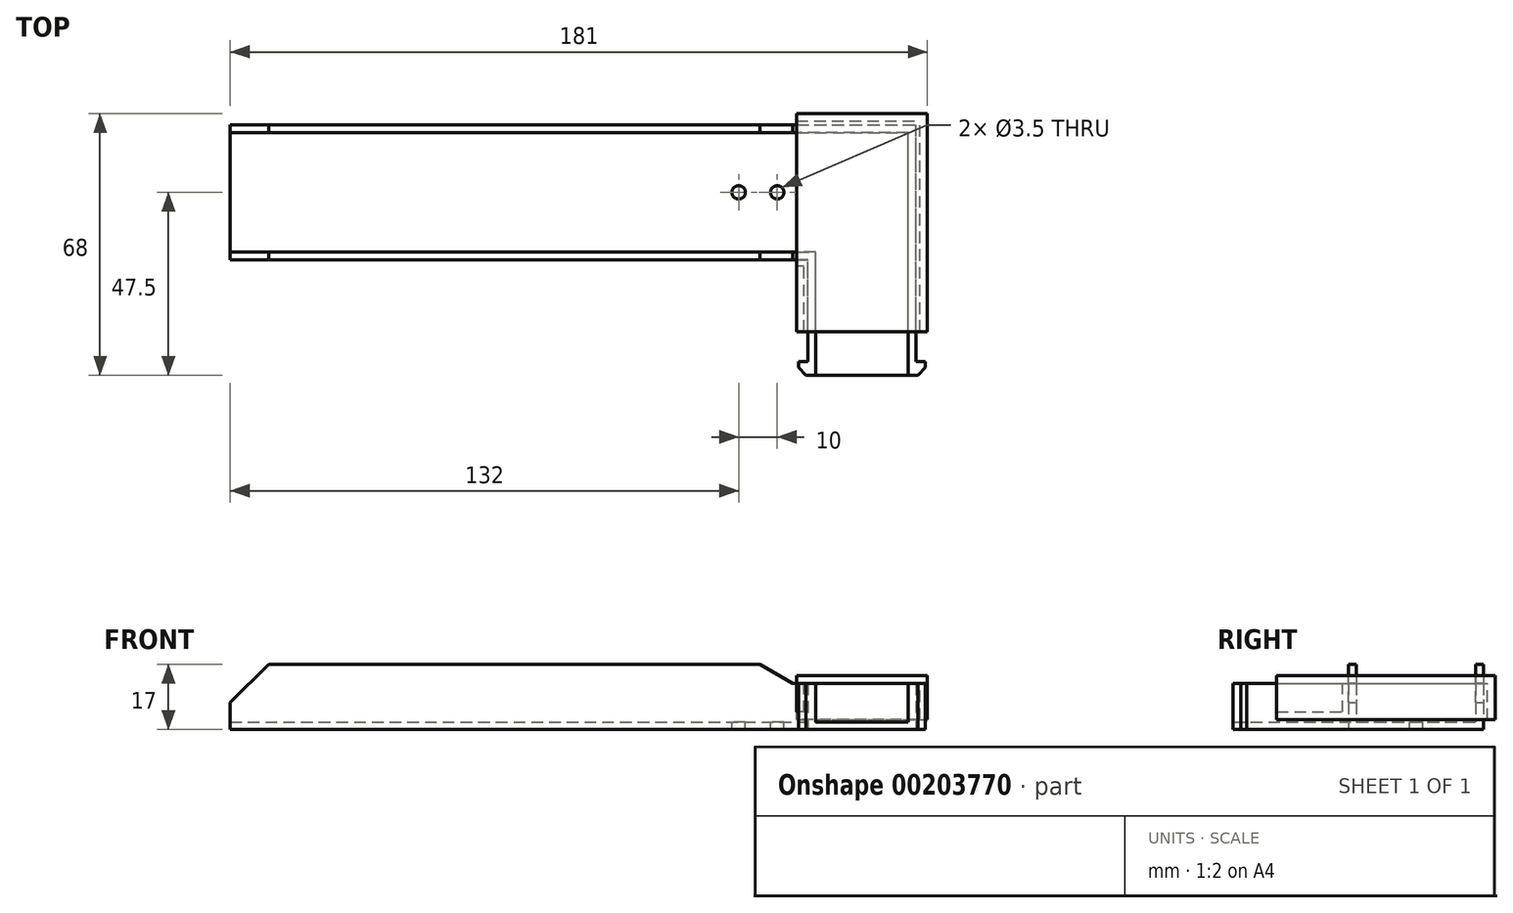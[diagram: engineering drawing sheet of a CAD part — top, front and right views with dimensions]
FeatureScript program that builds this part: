
annotation { "Feature Type Name" : "Feature", "Feature Type Description" : "" }
export const myFeature = defineFeature(function(context is Context, id is Id, definition is map)
    precondition{}
    {
        {
            var Q0;
            Q0=qCreatedBy(makeId("Top.planeOp"),FACE);
            var sketch = newSketch(context, id + "F0", { "sketchPlane" : qUnion([Q0])});
            skLineSegment(sketch, "E0", {"start": v(0, 0) * mm, "end": v(-14, 0) * mm});
            skLineSegment(sketch, "E1", {"start": v(-14, 0) * mm, "end": v(-14, 30) * mm});
            skLineSegment(sketch, "E2", {"start": v(-14, 30) * mm, "end": v(-164, 30) * mm});
            skLineSegment(sketch, "E3", {"start": v(-164, 30) * mm, "end": v(-164, 65) * mm});
            skLineSegment(sketch, "E4", {"start": v(-164, 65) * mm, "end": v(14, 65) * mm});
            skLineSegment(sketch, "E5", {"start": v(0, 0) * mm, "end": v(14, 0) * mm});
            skLineSegment(sketch, "E6", {"start": v(14, 0) * mm, "end": v(14, 65) * mm});
            skSolve(sketch);
        }
        {
            var Q0;
            Q0=makeQuery(id+"F0.imprint","IMPRINT",FACE,{"disambiguationData":[TD([[makeQuery(id+"F0.imprint","IMPRINT",EDGE,{"derivedFrom":sQuery(id+"F0.wireOp",EDGE,"E0")}),-1.0]])]});
            extrude(context, id + "F1", {"entities" : qUnion([Q0]), "depth" : 2 * mm, "offsetDistance" : 25 * mm});
        }
        {
            var Q0;
            Q0=makeQuery(id+"F1.opExtrude","CAP_FACE",FACE,{"disambiguationData":[OSD([sQuery(id+"F0.wireOp",EDGE,"E0"),sQuery(id+"F0.wireOp",EDGE,"E1"),sQuery(id+"F0.wireOp",EDGE,"E2"),sQuery(id+"F0.wireOp",EDGE,"E3"),sQuery(id+"F0.wireOp",EDGE,"E4"),sQuery(id+"F0.wireOp",EDGE,"E5"),sQuery(id+"F0.wireOp",EDGE,"E6")])],"isStart":false});
            var sketch = newSketch(context, id + "F2", { "sketchPlane" : qUnion([Q0])});
            skLineSegment(sketch, "E7", {"start": v(-14, 30) * mm, "end": v(-14, 0) * mm});
            skLineSegment(sketch, "E8", {"start": v(-14, 0) * mm, "end": v(-12, 0) * mm});
            skLineSegment(sketch, "E9", {"start": v(-12, 0) * mm, "end": v(-12, 30) * mm});
            skLineSegment(sketch, "E10", {"start": v(-12, 30) * mm, "end": v(-14, 30) * mm});
            skLineSegment(sketch, "E11", {"start": v(14, 65) * mm, "end": v(14, 0) * mm});
            skLineSegment(sketch, "E12", {"start": v(14, 0) * mm, "end": v(12, 0) * mm});
            skLineSegment(sketch, "E13", {"start": v(12, 0) * mm, "end": v(12, 65) * mm});
            skLineSegment(sketch, "E14", {"start": v(12, 65) * mm, "end": v(14, 65) * mm});
            skSolve(sketch);
        }
        {
            var Q0;
            Q0=makeQuery(id+"F2.imprint","IMPRINT",FACE,{"disambiguationData":[TD([[makeQuery(id+"F2.imprint","IMPRINT",EDGE,{"derivedFrom":sQuery(id+"F2.wireOp",EDGE,"E7")}),-1.0]])]});
            var Q1;
            Q1=makeQuery(id+"F2.imprint","IMPRINT",FACE,{"disambiguationData":[TD([[makeQuery(id+"F2.imprint","IMPRINT",EDGE,{"derivedFrom":sQuery(id+"F2.wireOp",EDGE,"E11")}),1.0]])]});
            extrude(context, id + "F3", {"entities" : qUnion([Q0, Q1]), "operationType" : NewBodyOperationType.ADD, "depth" : 10 * mm, "offsetDistance" : 25 * mm});
        }
        {
            var Q0;
            Q0=makeQuery(id+"F3.opExtrude","CAP_FACE",FACE,{"disambiguationData":[OSD([sQuery(id+"F2.wireOp",EDGE,"E7"),sQuery(id+"F2.wireOp",EDGE,"E8"),sQuery(id+"F2.wireOp",EDGE,"E9"),sQuery(id+"F2.wireOp",EDGE,"E10")])],"isStart":false});
            var sketch = newSketch(context, id + "F4", { "sketchPlane" : qUnion([Q0])});
            skLineSegment(sketch, "E15", {"start": v(0, 0) * mm, "end": v(0, -25.03) * mm, "construction": true});
            skLineSegment(sketch, "E16", {"start": v(-14, 0) * mm, "end": v(-14, 3.5) * mm});
            skLineSegment(sketch, "E17", {"start": v(-14, 3.5) * mm, "end": v(-16.5, 3.5) * mm});
            skLineSegment(sketch, "E18", {"start": v(-16.5, 3.5) * mm, "end": v(-16.5, 0) * mm});
            skLineSegment(sketch, "E19", {"start": v(-16.5, 0) * mm, "end": v(-14, 0) * mm});
            skLineSegment(sketch, "E20.MirrorCS", {"start": v(14, 0) * mm, "end": v(14, 3.5) * mm});
            skLineSegment(sketch, "E21.MirrorCS", {"start": v(14, 3.5) * mm, "end": v(16.5, 3.5) * mm});
            skLineSegment(sketch, "E22.MirrorCS", {"start": v(16.5, 0) * mm, "end": v(14, 0) * mm});
            skLineSegment(sketch, "E23.MirrorCS", {"start": v(16.5, 3.5) * mm, "end": v(16.5, 0) * mm});
            skSolve(sketch);
        }
        {
            var Q0;
            Q0=makeQuery(id+"F4.imprint","IMPRINT",FACE,{"disambiguationData":[TD([[makeQuery(id+"F4.imprint","IMPRINT",EDGE,{"derivedFrom":sQuery(id+"F4.wireOp",EDGE,"E16")}),1.0]])]});
            var Q1;
            Q1=makeQuery(id+"F4.imprint","IMPRINT",FACE,{"disambiguationData":[TD([[makeQuery(id+"F4.imprint","IMPRINT",EDGE,{"derivedFrom":sQuery(id+"F4.wireOp",EDGE,"E20.MirrorCS")}),-1.0]])]});
            extrude(context, id + "F5", {"entities" : qUnion([Q0, Q1]), "operationType" : NewBodyOperationType.ADD, "oppositeDirection" : true, "depth" : 12 * mm, "offsetDistance" : 25 * mm});
        }
        {
            var Q0;
            Q0=makeQuery(id+"F5.opExtrude","SWEPT_EDGE",EDGE,{"disambiguationData":[OSD([sQuery(id+"F4.wireOp",EDGE,"E18"),sQuery(id+"F4.wireOp",EDGE,"E19")])]});
            var Q1;
            Q1=makeQuery(id+"F5.opExtrude","SWEPT_EDGE",EDGE,{"disambiguationData":[OSD([sQuery(id+"F4.wireOp",EDGE,"E22.MirrorCS"),sQuery(id+"F4.wireOp",EDGE,"E23.MirrorCS")])]});
            chamfer(context, id + "F6", {"entities" : qUnion([Q0, Q1]), "width" : 2 * mm, "tangentPropagation" : true});
        }
        {
            var Q0;
            Q0=makeQuery(id+"F1.opExtrude","CAP_FACE",FACE,{"disambiguationData":[OSD([sQuery(id+"F0.wireOp",EDGE,"E0"),sQuery(id+"F0.wireOp",EDGE,"E1"),sQuery(id+"F0.wireOp",EDGE,"E2"),sQuery(id+"F0.wireOp",EDGE,"E3"),sQuery(id+"F0.wireOp",EDGE,"E4"),sQuery(id+"F0.wireOp",EDGE,"E5"),sQuery(id+"F0.wireOp",EDGE,"E6")])],"isStart":false});
            var sketch = newSketch(context, id + "F7", { "sketchPlane" : qUnion([Q0])});
            skLineSegment(sketch, "E24", {"start": v(12, 65) * mm, "end": v(-164, 65) * mm});
            skLineSegment(sketch, "E25", {"start": v(-164, 65) * mm, "end": v(-164, 63) * mm});
            skLineSegment(sketch, "E26", {"start": v(-164, 63) * mm, "end": v(12, 63) * mm});
            skLineSegment(sketch, "E27", {"start": v(12, 63) * mm, "end": v(12, 65) * mm});
            skLineSegment(sketch, "E28", {"start": v(-12, 30) * mm, "end": v(-164, 30) * mm});
            skLineSegment(sketch, "E29", {"start": v(-164, 30) * mm, "end": v(-164, 32) * mm});
            skLineSegment(sketch, "E30", {"start": v(-164, 32) * mm, "end": v(-12, 32) * mm});
            skLineSegment(sketch, "E31", {"start": v(-12, 32) * mm, "end": v(-12, 30) * mm});
            skSolve(sketch);
        }
        {
            var Q0;
            Q0=makeQuery(id+"F7.imprint","IMPRINT",FACE,{"disambiguationData":[TD([[makeQuery(id+"F7.imprint","IMPRINT",EDGE,{"derivedFrom":sQuery(id+"F7.wireOp",EDGE,"E24")}),-1.0]])]});
            var Q1;
            {var subQ0=sQuery(id+"F7.wireOp",EDGE,"E29");Q1=makeQuery(id+"F7.imprint","IMPRINT",FACE,{"disambiguationData":[TD([[makeQuery(id+"F7.imprint","IMPRINT",EDGE,{"derivedFrom":subQ0}),-1.0]])]});}
            extrude(context, id + "F8", {"entities" : qUnion([Q0, Q1]), "operationType" : NewBodyOperationType.ADD, "depth" : 15 * mm, "offsetDistance" : 25 * mm});
        }
        {
            var Q0;
            Q0=makeQuery(id+"F8.opExtrude","CAP_EDGE",EDGE,{"disambiguationData":[OSD([sQuery(id+"F7.wireOp",EDGE,"E25")])],"isStart":false});
            var Q1;
            Q1=makeQuery(id+"F8.opExtrude","CAP_EDGE",EDGE,{"disambiguationData":[OSD([sQuery(id+"F7.wireOp",EDGE,"E29")])],"isStart":false});
            chamfer(context, id + "F9", {"entities" : qUnion([Q0, Q1]), "width" : 10 * mm, "tangentPropagation" : true});
        }
        {
            var Q0;
            Q0=makeQuery(id+"F1.opExtrude","CAP_FACE",FACE,{"disambiguationData":[OSD([sQuery(id+"F0.wireOp",EDGE,"E0"),sQuery(id+"F0.wireOp",EDGE,"E1"),sQuery(id+"F0.wireOp",EDGE,"E2"),sQuery(id+"F0.wireOp",EDGE,"E3"),sQuery(id+"F0.wireOp",EDGE,"E4"),sQuery(id+"F0.wireOp",EDGE,"E5"),sQuery(id+"F0.wireOp",EDGE,"E6")])],"isStart":false});
            var sketch = newSketch(context, id + "F10", { "sketchPlane" : qUnion([Q0])});
            skLineSegment(sketch, "E32", {"start": v(-12, 32) * mm, "end": v(-12, 63) * mm, "construction": true});
            skLineSegment(sketch, "E33", {"start": v(-12, 47.5) * mm, "end": v(-22, 47.5) * mm, "construction": true});
            skLineSegment(sketch, "E34", {"start": v(-22, 47.5) * mm, "end": v(-32, 47.5) * mm, "construction": true});
            skCircle(sketch, "E35", {"center": v(-22, 47.5) * mm, "radius": 1.75 * mm});
            skCircle(sketch, "E36", {"center": v(-32, 47.5) * mm, "radius": 1.75 * mm});
            skSolve(sketch);
        }
        {
            var Q0;
            Q0=makeQuery(id+"F10.imprint","IMPRINT",FACE,{"disambiguationData":[TD([[makeQuery(id+"F10.imprint","IMPRINT",EDGE,{"derivedFrom":sQuery(id+"F10.wireOp",EDGE,"E36")}),1.0]])]});
            var Q1;
            Q1=makeQuery(id+"F10.imprint","IMPRINT",FACE,{"disambiguationData":[TD([[makeQuery(id+"F10.imprint","IMPRINT",EDGE,{"derivedFrom":sQuery(id+"F10.wireOp",EDGE,"E35")}),1.0]])]});
            extrude(context, id + "F11", {"entities" : qUnion([Q0, Q1]), "operationType" : NewBodyOperationType.REMOVE, "endBound" : BoundingType.UP_TO_NEXT, "oppositeDirection" : true, "depth" : 25 * mm, "offsetDistance" : 25 * mm});
        }
        {
            var Q0;
            Q0=makeQuery(id+"F8.boolean.opBoolean","MERGE",FACE,{"derivedFrom":[makeQuery(id+"F1.opExtrude","SWEPT_FACE",FACE,{"disambiguationData":[OSD([sQuery(id+"F0.wireOp",EDGE,"E2")])]}),makeQuery(id+"F8.opExtrude","SWEPT_FACE",FACE,{"disambiguationData":[OSD([sQuery(id+"F7.wireOp",EDGE,"E28")])]})]});
            var sketch = newSketch(context, id + "F12", { "sketchPlane" : qUnion([Q0])});
            skLineSegment(sketch, "E37", {"start": v(-12, 12) * mm, "end": v(12, 12) * mm});
            skLineSegment(sketch, "E38", {"start": v(12, 12) * mm, "end": v(12, 17) * mm});
            skLineSegment(sketch, "E39", {"start": v(12, 17) * mm, "end": v(-18, 17) * mm});
            skLineSegment(sketch, "E40", {"start": v(-18, 12) * mm, "end": v(-12, 12) * mm});
            skLineSegment(sketch, "E41", {"start": v(-18, 12) * mm, "end": v(-26.49, 17) * mm});
            skLineSegment(sketch, "E42", {"start": v(-26.49, 17) * mm, "end": v(-18, 17) * mm});
            skSolve(sketch);
        }
        {
            var Q0;
            Q0=makeQuery(id+"F12.imprint","IMPRINT",FACE,{"disambiguationData":[TD([[makeQuery(id+"F12.imprint","IMPRINT",EDGE,{"derivedFrom":sQuery(id+"F12.wireOp",EDGE,"E37")}),1.0]])]});
            var Q1;
            {var subQ0=sQuery(id+"F12.wireOp",EDGE,"E41");Q1=makeQuery(id+"F12.imprint","IMPRINT",FACE,{"disambiguationData":[TD([[makeQuery(id+"F12.imprint","IMPRINT",EDGE,{"derivedFrom":subQ0}),-1.0]])]});}
            extrude(context, id + "F13", {"entities" : qUnion([Q0, Q1]), "operationType" : NewBodyOperationType.REMOVE, "endBound" : BoundingType.THROUGH_ALL, "oppositeDirection" : true, "depth" : 25 * mm, "offsetDistance" : 25 * mm});
        }
        {
            var Q0;
            Q0=makeQuery(id+"F13.boolean.opBoolean","MERGE",FACE,{"derivedFrom":[makeQuery(id+"F5.boolean.opBoolean","MERGE",FACE,{"derivedFrom":[makeQuery(id+"F3.opExtrude","CAP_FACE",FACE,{"disambiguationData":[OSD([sQuery(id+"F2.wireOp",EDGE,"E7"),sQuery(id+"F2.wireOp",EDGE,"E8"),sQuery(id+"F2.wireOp",EDGE,"E9"),sQuery(id+"F2.wireOp",EDGE,"E10")])],"isStart":false}),makeQuery(id+"F5.opExtrude","CAP_FACE",FACE,{"disambiguationData":[OSD([sQuery(id+"F4.wireOp",EDGE,"E16"),sQuery(id+"F4.wireOp",EDGE,"E17"),sQuery(id+"F4.wireOp",EDGE,"E18"),sQuery(id+"F4.wireOp",EDGE,"E19")])],"isStart":true})]}),makeQuery(id+"F13.opExtrude","SWEPT_FACE",FACE,{"disambiguationData":[OSD([sQuery(id+"F12.wireOp",EDGE,"E37"),sQuery(id+"F12.wireOp",EDGE,"E40")])]})]});
            var sketch = newSketch(context, id + "F14", { "sketchPlane" : qUnion([Q0])});
            skLineSegment(sketch, "E43.0", {"start": v(-17, 68) * mm, "end": v(17, 68) * mm});
            skLineSegment(sketch, "E43.1", {"start": v(-17, 11.32) * mm, "end": v(-17, 68) * mm});
            skLineSegment(sketch, "E43.3", {"start": v(17, 11.32) * mm, "end": v(17, 68) * mm});
            skPoint(sketch, "E44.orphan", {"position": v(-17, 4.32) * mm});
            skLineSegment(sketch, "E45", {"start": v(-17, 11.32) * mm, "end": v(17, 11.32) * mm});
            skSolve(sketch);
        }
        {
            var Q0;
            {var subQ0=sQuery(id+"F14.wireOp",EDGE,"RSVECKuP-vbVK-7Mtd-HKy0-AH4jZLgJ3iUv");var subQ1=sQuery(id+"F14.wireOp",EDGE,"E43.1");var subQ2=makeQuery(id+"F14.imprint","INTERSECT",VERTEX,{"derivedFrom":[subQ1,subQ0]});Q0=makeQuery(id+"F14.imprint","IMPRINT",FACE,{"disambiguationData":[TD([[makeQuery(id+"F14.imprint","IMPRINT",EDGE,{"disambiguationData":[TD([[subQ2,-1.0]])],"derivedFrom":subQ0}),1.0]])]});}
            var Q1;
            {var subQ8=sQuery(id+"F14.wireOp",EDGE,"E43.0");Q1=makeQuery(id+"F14.imprint","IMPRINT",FACE,{"disambiguationData":[TD([[makeQuery(id+"F14.imprint","IMPRINT",EDGE,{"derivedFrom":subQ8}),-1.0]])]});}
            var Q2;
            {var subQ0=sQuery(id+"F14.wireOp",EDGE,"E45");var subQ1=sQuery(id+"F14.wireOp",EDGE,"E43.1");var subQ2=makeQuery(id+"F14.imprint","INTERSECT",VERTEX,{"derivedFrom":[subQ1,subQ0]});Q2=makeQuery(id+"F14.imprint","IMPRINT",FACE,{"disambiguationData":[TD([[makeQuery(id+"F14.imprint","IMPRINT",EDGE,{"disambiguationData":[TD([[subQ2,-1.0]])],"derivedFrom":subQ0}),1.0]])]});}
            var Q3;
            {var subQ3=makeQuery(id+"F3.opExtrude","CAP_EDGE",EDGE,{"disambiguationData":[OSD([sQuery(id+"F2.wireOp",EDGE,"E7")])],"isStart":false});var subQ5=sQuery(id+"F14.wireOp",EDGE,"E45");var subQ6=makeQuery(id+"F14.imprint","INTERSECT",VERTEX,{"derivedFrom":[subQ3,subQ5]});Q3=makeQuery(id+"F14.imprint","IMPRINT",FACE,{"disambiguationData":[TD([[makeQuery(id+"F14.imprint","IMPRINT",EDGE,{"disambiguationData":[TD([[subQ6,-1.0]])],"derivedFrom":subQ3}),-1.0]])]});}
            extrude(context, id + "F15", {"entities" : qUnion([Q0, Q1, Q2, Q3]), "depth" : 2 * mm, "offsetDistance" : 25 * mm});
        }
        {
            var Q0;
            Q0=makeQuery(id+"F15.opExtrude","SWEPT_FACE",FACE,{"disambiguationData":[OSD([sQuery(id+"F14.wireOp",EDGE,"E43.1")])]});
            var sketch = newSketch(context, id + "F16", { "sketchPlane" : qUnion([Q0])});
            skLineSegment(sketch, "E46", {"start": v(-11.32, 4.59) * mm, "end": v(-28.39, 4.59) * mm});
            skLineSegment(sketch, "E47", {"start": v(-28.39, 4.59) * mm, "end": v(-28.39, 12) * mm});
            skLineSegment(sketch, "E48", {"start": v(-28.39, 12) * mm, "end": v(-11.32, 12) * mm});
            skLineSegment(sketch, "E49", {"start": v(-11.32, 4.59) * mm, "end": v(-11.32, 12) * mm});
            skSolve(sketch);
        }
        {
            var Q0;
            Q0=makeQuery(id+"F16.imprint","IMPRINT",FACE,{"disambiguationData":[TD([[makeQuery(id+"F16.imprint","IMPRINT",EDGE,{"derivedFrom":sQuery(id+"F16.wireOp",EDGE,"E46")}),-1.0]])]});
            extrude(context, id + "F17", {"entities" : qUnion([Q0]), "operationType" : NewBodyOperationType.ADD, "oppositeDirection" : true, "depth" : 2 * mm, "offsetDistance" : 25 * mm});
        }
        {
            var Q0;
            Q0=makeQuery(id+"F15.opExtrude","SWEPT_FACE",FACE,{"disambiguationData":[OSD([sQuery(id+"F14.wireOp",EDGE,"E43.3")])]});
            var sketch = newSketch(context, id + "F18", { "sketchPlane" : qUnion([Q0])});
            skLineSegment(sketch, "E50", {"start": v(68, 12) * mm, "end": v(11.32, 12) * mm});
            skLineSegment(sketch, "E51", {"start": v(11.32, 2.58) * mm, "end": v(68, 2.58) * mm});
            skLineSegment(sketch, "E52", {"start": v(68, 2.58) * mm, "end": v(68, 12) * mm});
            skLineSegment(sketch, "E53", {"start": v(11.32, 2.58) * mm, "end": v(11.32, 12) * mm});
            skSolve(sketch);
        }
        {
            var Q0;
            Q0=makeQuery(id+"F18.imprint","IMPRINT",FACE,{"disambiguationData":[TD([[makeQuery(id+"F18.imprint","IMPRINT",EDGE,{"derivedFrom":sQuery(id+"F18.wireOp",EDGE,"E50")}),-1.0]])]});
            extrude(context, id + "F19", {"entities" : qUnion([Q0]), "operationType" : NewBodyOperationType.ADD, "oppositeDirection" : true, "depth" : 2 * mm, "offsetDistance" : 25 * mm});
        }
        {
            var Q0;
            Q0=makeQuery(id+"F19.boolean.opBoolean","MERGE",FACE,{"derivedFrom":[makeQuery(id+"F15.opExtrude","SWEPT_FACE",FACE,{"disambiguationData":[OSD([sQuery(id+"F14.wireOp",EDGE,"E43.0")])]}),makeQuery(id+"F19.opExtrude","SWEPT_FACE",FACE,{"disambiguationData":[OSD([sQuery(id+"F18.wireOp",EDGE,"E52")])]})]});
            var sketch = newSketch(context, id + "F20", { "sketchPlane" : qUnion([Q0])});
            skLineSegment(sketch, "E54", {"start": v(17, 12) * mm, "end": v(-15, 12) * mm});
            skLineSegment(sketch, "E55", {"start": v(-15, 12) * mm, "end": v(-15, 2.58) * mm});
            skLineSegment(sketch, "E56", {"start": v(-15, 2.58) * mm, "end": v(17, 2.58) * mm});
            skLineSegment(sketch, "E57", {"start": v(17, 2.58) * mm, "end": v(17, 12) * mm});
            skSolve(sketch);
        }
        {
            var Q0;
            Q0=makeQuery(id+"F20.imprint","IMPRINT",FACE,{"disambiguationData":[TD([[makeQuery(id+"F20.imprint","IMPRINT",EDGE,{"derivedFrom":sQuery(id+"F20.wireOp",EDGE,"E54")}),1.0]])]});
            extrude(context, id + "F21", {"entities" : qUnion([Q0]), "operationType" : NewBodyOperationType.ADD, "oppositeDirection" : true, "depth" : 2 * mm, "offsetDistance" : 25 * mm});
        }
    });
